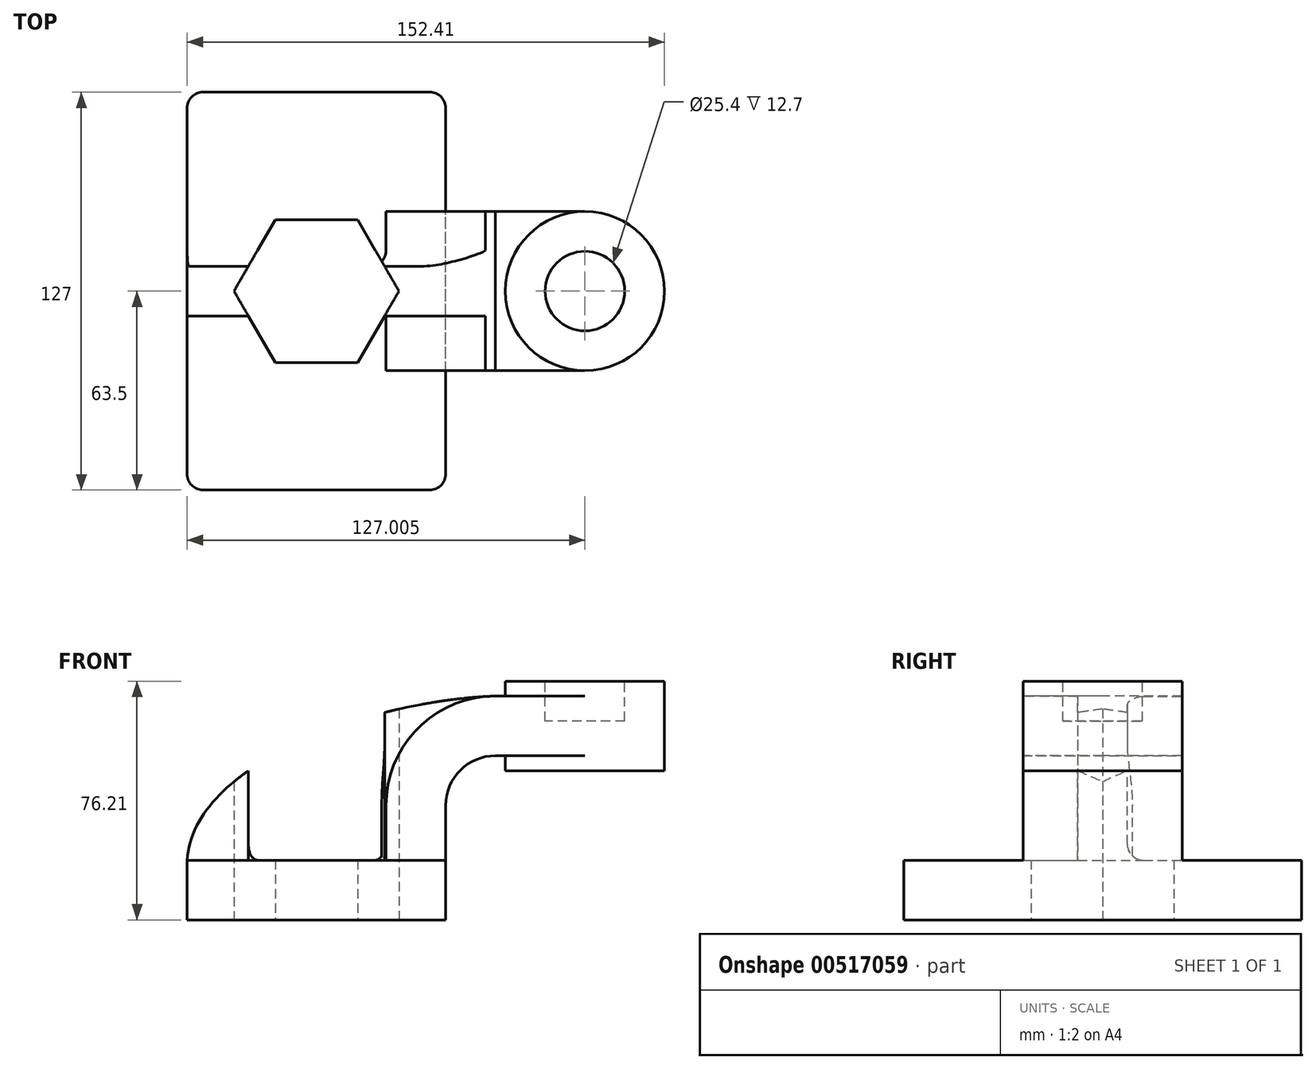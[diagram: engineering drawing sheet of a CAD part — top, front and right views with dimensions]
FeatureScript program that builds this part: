
annotation { "Feature Type Name" : "Feature", "Feature Type Description" : "" }
export const myFeature = defineFeature(function(context is Context, id is Id, definition is map)
    precondition{}
    {
        {
            var Q0;
            Q0=qCreatedBy(makeId("Front.planeOp"),FACE);
            var sketch = newSketch(context, id + "F0", { "sketchPlane" : qUnion([Q0])});
            skLineSegment(sketch, "E0.rect.bottom", {"start": v(-41.28, 9.52) * mm, "end": v(41.28, 9.52) * mm});
            skLineSegment(sketch, "E0.rect.top", {"start": v(-41.28, -9.52) * mm, "end": v(41.28, -9.52) * mm});
            skLineSegment(sketch, "E0.rect.left", {"start": v(-41.28, 9.52) * mm, "end": v(-41.28, -9.52) * mm});
            skLineSegment(sketch, "E0.rect.right", {"start": v(41.28, 9.52) * mm, "end": v(41.28, -9.52) * mm});
            skPoint(sketch, "E0.rect.middle", {"position": v(0, 0) * mm});
            skLineSegment(sketch, "E1", {"start": v(41.28, 9.52) * mm, "end": v(41.28, 27) * mm});
            skArc(sketch, "E2", {"start": v(41.28, 27) * mm, "mid": v(45.92, 38.23) * mm, "end": v(57.15, 42.88) * mm});
            skLineSegment(sketch, "E3", {"start": v(57.15, 42.88) * mm, "end": v(85.72, 42.88) * mm});
            skLineSegment(sketch, "E4.rect.bottom", {"start": v(60.32, 38.1) * mm, "end": v(111.12, 38.1) * mm});
            skLineSegment(sketch, "E4.rect.top", {"start": v(60.32, 66.68) * mm, "end": v(111.12, 66.68) * mm});
            skLineSegment(sketch, "E4.rect.left", {"start": v(60.32, 38.1) * mm, "end": v(60.32, 66.68) * mm});
            skLineSegment(sketch, "E4.rect.right", {"start": v(111.13, 38.1) * mm, "end": v(111.12, 66.68) * mm});
            skPoint(sketch, "E4.rect.middle", {"position": v(85.72, 52.39) * mm});
            skLineSegment(sketch, "E5.0", {"start": v(57.15, 61.93) * mm, "end": v(85.72, 61.93) * mm});
            skArc(sketch, "E5.1", {"start": v(22.23, 27) * mm, "mid": v(32.45, 51.7) * mm, "end": v(57.15, 61.93) * mm});
            skLineSegment(sketch, "E5.2", {"start": v(22.23, 9.52) * mm, "end": v(22.23, 27) * mm});
            skLineSegment(sketch, "E6", {"start": v(85.72, 38.1) * mm, "end": v(85.72, 66.68) * mm});
            skFitSpline(sketch, "E7", {"points": [v(-41.28, 9.53) * mm, v(57.15, 61.93) * mm], "startDerivative": vector(5.2, 92.34) * mm, "endDerivative": vector(120.92, 4.22) * mm});
            skSolve(sketch);
        }
        {
            var Q0;
            Q0=makeQuery(id+"F0.imprint","IMPRINT",FACE,{"disambiguationData":[TD([[makeQuery(id+"F0.imprint","IMPRINT",EDGE,{"derivedFrom":sQuery(id+"F0.wireOp",EDGE,"E0.rect.top")}),1.0]])]});
            extrude(context, id + "F1", {"entities" : qUnion([Q0]), "endBound" : BoundingType.SYMMETRIC, "depth" : 127 * mm});
        }
        {
            var Q0;
            {var subQ9=sQuery(id+"F0.wireOp",EDGE,"E1");Q0=makeQuery(id+"F0.imprint","IMPRINT",FACE,{"disambiguationData":[TD([[makeQuery(id+"F0.imprint","IMPRINT",EDGE,{"derivedFrom":subQ9}),1.0]])]});}
            var Q1;
            {var subQ0=sQuery(id+"F0.wireOp",EDGE,"E6");var subQ1=sQuery(id+"F0.wireOp",EDGE,"E3");var subQ2=makeQuery(id+"F0.imprint","INTERSECT",VERTEX,{"derivedFrom":[subQ1,subQ0]});Q1=makeQuery(id+"F0.imprint","IMPRINT",FACE,{"disambiguationData":[TD([[makeQuery(id+"F0.imprint","IMPRINT",EDGE,{"disambiguationData":[TD([[subQ2,1.0]])],"derivedFrom":subQ1}),1.0]])]});}
            extrude(context, id + "F2", {"entities" : qUnion([Q0, Q1]), "operationType" : NewBodyOperationType.ADD, "endBound" : BoundingType.SYMMETRIC, "depth" : 50.8 * mm});
        }
        {
            var Q0;
            {var subQ3=sQuery(id+"F0.wireOp",EDGE,"E5.2");Q0=makeQuery(id+"F0.imprint","IMPRINT",FACE,{"disambiguationData":[TD([[makeQuery(id+"F0.imprint","IMPRINT",EDGE,{"derivedFrom":subQ3}),1.0]])]});}
            extrude(context, id + "F3", {"entities" : qUnion([Q0]), "operationType" : NewBodyOperationType.ADD, "endBound" : BoundingType.SYMMETRIC, "depth" : 15.88 * mm});
        }
        {
            var Q0;
            {var subQ5=sQuery(id+"F0.wireOp",EDGE,"E4.rect.right");Q0=makeQuery(id+"F0.imprint","IMPRINT",FACE,{"disambiguationData":[TD([[makeQuery(id+"F0.imprint","IMPRINT",EDGE,{"derivedFrom":subQ5}),1.0]])]});}
            var Q1;
            Q1=sQuery(id+"F0.wireOp",EDGE,"E6");
            revolve(context, id + "F4", {"operationType" : NewBodyOperationType.ADD, "entities" : qUnion([Q0]), "axis" : qUnion([Q1]), "revolveType" : RevolveType.FULL});
        }
        {
            var Q0;
            Q0=makeQuery(id+"F1.opExtrude","CAP_EDGE",EDGE,{"disambiguationData":[OSD([sQuery(id+"F0.wireOp",EDGE,"E0.rect.right")])],"isStart":false});
            var Q1;
            Q1=makeQuery(id+"F1.opExtrude","CAP_EDGE",EDGE,{"disambiguationData":[OSD([sQuery(id+"F0.wireOp",EDGE,"E0.rect.left")])],"isStart":false});
            var Q2;
            Q2=makeQuery(id+"F1.opExtrude","CAP_EDGE",EDGE,{"disambiguationData":[OSD([sQuery(id+"F0.wireOp",EDGE,"E0.rect.right")])],"isStart":true});
            var Q3;
            Q3=makeQuery(id+"F1.opExtrude","CAP_EDGE",EDGE,{"disambiguationData":[OSD([sQuery(id+"F0.wireOp",EDGE,"E0.rect.left")])],"isStart":true});
            fillet(context, id + "F5", {"entities" : qUnion([Q0, Q1, Q2, Q3]), "radius" : 5.08 * mm, "tangentPropagation" : true, "allowEdgeOverflow" : false});
        }
        {
            var Q0;
            Q0=makeQuery(id+"F4.opRevolve","SWEPT_FACE",FACE,{"disambiguationData":[OSD([sQuery(id+"F0.wireOp",EDGE,"E4.rect.top")])]});
            var sketch = newSketch(context, id + "F6", { "sketchPlane" : qUnion([Q0])});
            skCircle(sketch, "E8", {"center": v(85.72, 0) * mm, "radius": 12.7 * mm});
            skSolve(sketch);
        }
        {
            var Q0;
            Q0=makeQuery(id+"F6.imprint","IMPRINT",FACE,{"disambiguationData":[TD([[makeQuery(id+"F6.imprint","IMPRINT",EDGE,{"derivedFrom":sQuery(id+"F6.wireOp",EDGE,"E8")}),1.0]])]});
            extrude(context, id + "F7", {"entities" : qUnion([Q0]), "operationType" : NewBodyOperationType.REMOVE, "oppositeDirection" : true, "depth" : 12.7 * mm});
        }
        {
            var Q0;
            Q0=makeQuery(id+"F3.opExtrude","CAP_EDGE",EDGE,{"disambiguationData":[OSD([sQuery(id+"F0.wireOp",EDGE,"E5.1")])],"isStart":false});
            var Q1;
            Q1=makeQuery(id+"F3.opExtrude","CAP_EDGE",EDGE,{"disambiguationData":[OSD([sQuery(id+"F0.wireOp",EDGE,"E5.2")])],"isStart":false});
            var Q2;
            Q2=makeQuery(id+"F3.opExtrude","CAP_EDGE",EDGE,{"disambiguationData":[OSD([sQuery(id+"F0.wireOp",EDGE,"E5.1")])],"isStart":true});
            var Q3;
            Q3=makeQuery(id+"F3.opExtrude","CAP_EDGE",EDGE,{"disambiguationData":[OSD([sQuery(id+"F0.wireOp",EDGE,"E5.2")])],"isStart":true});
            var Q4;
            Q4=makeQuery(id+"F3.opExtrude","CAP_EDGE",EDGE,{"disambiguationData":[OSD([sQuery(id+"F0.wireOp",EDGE,"E0.rect.bottom")])],"isStart":true});
            var Q5;
            Q5=makeQuery(id+"F3.opExtrude","CAP_EDGE",EDGE,{"disambiguationData":[OSD([sQuery(id+"F0.wireOp",EDGE,"E0.rect.bottom")])],"isStart":false});
            fillet(context, id + "F8", {"entities" : qUnion([Q0, Q1, Q2, Q3, Q4, Q5]), "radius" : 5.08 * mm, "tangentPropagation" : true, "allowEdgeOverflow" : false});
        }
        {
            var Q0;
            Q0=makeQuery(id+"F1.opExtrude","SWEPT_FACE",FACE,{"disambiguationData":[OSD([sQuery(id+"F0.wireOp",EDGE,"E0.rect.top")])]});
            var sketch = newSketch(context, id + "F9", { "sketchPlane" : qUnion([Q0])});
            skCircle(sketch, "E9.cCircle", {"center": v(0, 0) * mm, "radius": 22.8 * mm, "construction": true});
            skLineSegment(sketch, "E9.0", {"start": v(-13.16, 22.8) * mm, "end": v(13.16, 22.8) * mm});
            skLineSegment(sketch, "E9.1", {"start": v(13.16, 22.8) * mm, "end": v(26.33, 0) * mm});
            skLineSegment(sketch, "E9.2", {"start": v(26.33, 0) * mm, "end": v(13.16, -22.8) * mm});
            skLineSegment(sketch, "E9.3", {"start": v(13.16, -22.8) * mm, "end": v(-13.16, -22.8) * mm});
            skLineSegment(sketch, "E9.4", {"start": v(-13.16, -22.8) * mm, "end": v(-26.33, 0) * mm});
            skLineSegment(sketch, "E9.5", {"start": v(-26.33, 0) * mm, "end": v(-13.16, 22.8) * mm});
            skPoint(sketch, "E9.0.midPoint", {"position": v(0, 22.8) * mm});
            skSolve(sketch);
        }
        {
            var Q0;
            Q0=makeQuery(id+"F9.imprint","IMPRINT",FACE,{"disambiguationData":[TD([[makeQuery(id+"F9.imprint","IMPRINT",EDGE,{"derivedFrom":sQuery(id+"F9.wireOp",EDGE,"E9.0")}),-1.0]])]});
            extrude(context, id + "F10", {"entities" : qUnion([Q0]), "operationType" : NewBodyOperationType.REMOVE, "oppositeDirection" : true, "depth" : 90.42 * mm, "offsetDistance" : 25.4 * mm});
        }
    });
